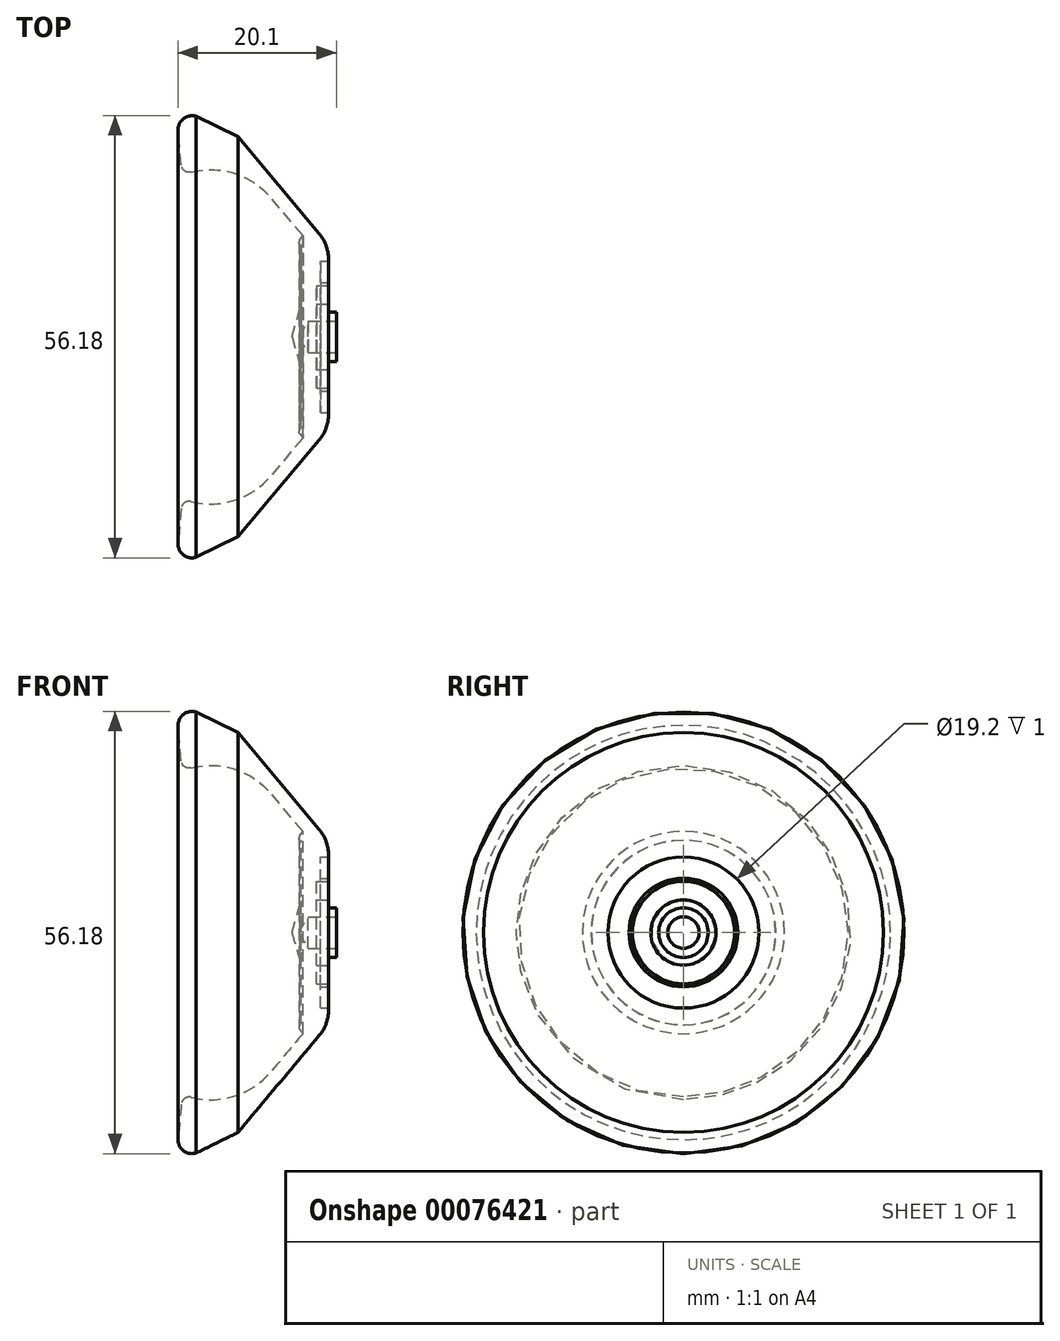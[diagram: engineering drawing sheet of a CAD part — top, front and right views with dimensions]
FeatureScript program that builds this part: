
annotation { "Feature Type Name" : "Feature", "Feature Type Description" : "" }
export const myFeature = defineFeature(function(context is Context, id is Id, definition is map)
    precondition{}
    {
        {
            var Q0;
            Q0=qCreatedBy(makeId("Front.planeOp"),FACE);
            var sketch = newSketch(context, id + "F0", { "sketchPlane" : qUnion([Q0])});
            skLineSegment(sketch, "E0", {"start": v(-1.4, 2) * mm, "end": v(-5, 2) * mm});
            skLineSegment(sketch, "E1", {"start": v(-5, 2) * mm, "end": v(-6.15, 0) * mm});
            skLineSegment(sketch, "E2", {"start": v(-6.15, 0) * mm, "end": v(-7.05, 0) * mm});
            skLineSegment(sketch, "E3", {"start": v(-5.65, 12.85) * mm, "end": v(-9.7, 17.66) * mm});
            skLineSegment(sketch, "E4", {"start": v(-1.4, 3.15) * mm, "end": v(-2.4, 3.15) * mm});
            skLineSegment(sketch, "E5", {"start": v(-2.4, 3.15) * mm, "end": v(-2.4, 4.15) * mm});
            skLineSegment(sketch, "E6", {"start": v(-2.4, 4.15) * mm, "end": v(-3.9, 4.15) * mm});
            skLineSegment(sketch, "E7", {"start": v(-3.9, 4.15) * mm, "end": v(-3.9, 6.5) * mm});
            skLineSegment(sketch, "E8", {"start": v(-3.9, 6.5) * mm, "end": v(-2.4, 6.5) * mm});
            skLineSegment(sketch, "E9", {"start": v(-2.4, 6.5) * mm, "end": v(-2.4, 6.9) * mm});
            skLineSegment(sketch, "E10", {"start": v(-2.4, 6.9) * mm, "end": v(-3.4, 6.9) * mm});
            skLineSegment(sketch, "E11", {"start": v(-3.4, 6.9) * mm, "end": v(-3.4, 9.6) * mm});
            skLineSegment(sketch, "E12", {"start": v(-3.4, 9.6) * mm, "end": v(-2.4, 9.6) * mm});
            skLineSegment(sketch, "E13", {"start": v(-2.4, 9.6) * mm, "end": v(-2.4, 9.87) * mm});
            skLineSegment(sketch, "E14", {"start": v(-1.4, 3.15) * mm, "end": v(-1.4, 2) * mm});
            skLineSegment(sketch, "E15", {"start": v(-13.9, 25.4) * mm, "end": v(-3.57, 13.09) * mm});
            skLineSegment(sketch, "E16", {"start": v(-5.9, 4) * mm, "end": v(-5.9, 11.48) * mm});
            skPoint(sketch, "E17.visualSharp", {"position": v(-2.4, 11.7) * mm});
            skArc(sketch, "E17.filletArc", {"start": v(-2.4, 9.87) * mm, "mid": v(-2.7, 11.58) * mm, "end": v(-3.57, 13.09) * mm});
            skLineSegment(sketch, "E18", {"start": v(-6, 11.7) * mm, "end": v(-6.02, 11.73) * mm});
            skLineSegment(sketch, "E19", {"start": v(-6.08, 12.27) * mm, "end": v(-5.65, 12.85) * mm});
            skPoint(sketch, "E20.visualSharp", {"position": v(-5.9, 11.64) * mm});
            skArc(sketch, "E20.filletArc", {"start": v(-5.9, 11.48) * mm, "mid": v(-5.93, 11.62) * mm, "end": v(-6.02, 11.73) * mm});
            skPoint(sketch, "E21.visualSharp", {"position": v(-6.32, 11.94) * mm});
            skArc(sketch, "E21.filletArc", {"start": v(-6.08, 12.27) * mm, "mid": v(-6.15, 11.97) * mm, "end": v(-6, 11.7) * mm});
            skLineSegment(sketch, "E22", {"start": v(-13.9, 25.4) * mm, "end": v(-19.2, 28) * mm});
            skArc(sketch, "E23", {"start": v(-19.2, 28) * mm, "mid": v(-20.78, 27.75) * mm, "end": v(-21.5, 26.32) * mm});
            skPoint(sketch, "E24.visualSharp", {"position": v(-15.6, 24.7) * mm});
            skArc(sketch, "E24.filletArc", {"start": v(-9.7, 17.66) * mm, "mid": v(-14.3, 20.76) * mm, "end": v(-19.85, 20.92) * mm});
            skLineSegment(sketch, "E25", {"start": v(-21.5, 26.32) * mm, "end": v(-21.1, 21.8) * mm});
            skPoint(sketch, "E26.visualSharp", {"position": v(-19.27, 1.42) * mm});
            skArc(sketch, "E26.filletArc", {"start": v(-21.1, 21.8) * mm, "mid": v(-20.68, 21.07) * mm, "end": v(-19.85, 20.92) * mm});
            skLineSegment(sketch, "E27", {"start": v(-7.05, 0) * mm, "end": v(-5.9, 4) * mm});
            skSolve(sketch);
        }
        {
            var Q0;
            Q0=qSketchRegion(id+"F0",true);
            var Q1;
            Q1=sQuery(id+"F0.wireOp",EDGE,"E2");
            revolve(context, id + "F1", {"entities" : qUnion([Q0]), "axis" : qUnion([Q1]), "revolveType" : RevolveType.FULL});
        }
    });
